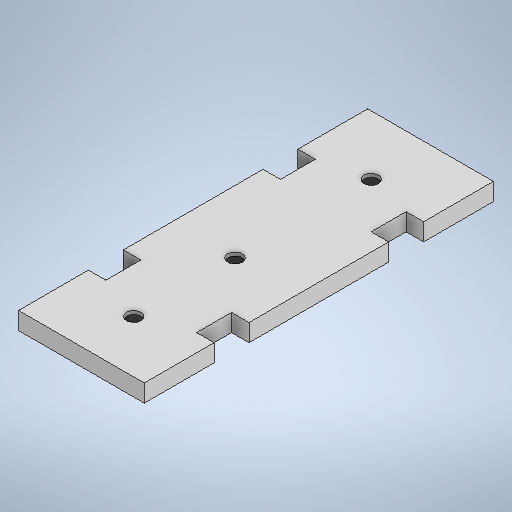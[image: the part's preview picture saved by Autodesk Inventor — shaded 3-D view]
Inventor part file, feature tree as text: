
AUTODESK INVENTOR PART (.ipt)
format: ipt  version: 2025.2 (Build 292293000, 293)  size: 267,776 bytes
history: native  units: mm
features: extrude x2, sketch x2
ambient origin geometry x8: Origin, YZ Plane, XZ Plane, XY Plane, X Axis, Y Axis, Z Axis, Center Point
bodies: Solid1 (feature_tree)
feature tree (4):
  extrude  "Extrusion1"  Depth=100.0mm
  extrude  "Extrusion2"  Depth=20.0mm
  sketch  "Sketch2"  dims[d0=36.0mm d1=100.0mm]
  sketch  "Sketch3"  dims[d2=20.0mm d3=20.0mm d4=10.0mm d5=5.0mm d6=10.0mm d7=5.0mm d8=5.0mm d9=15.0mm d11=29.0mm d12=10.1mm d13=39.0mm d14=10.1mm d15=5.0mm d16=0.0mm d18=4.2mm d19=4.2mm d20=4.2mm d21=1.0mm d22=0.0mm]
